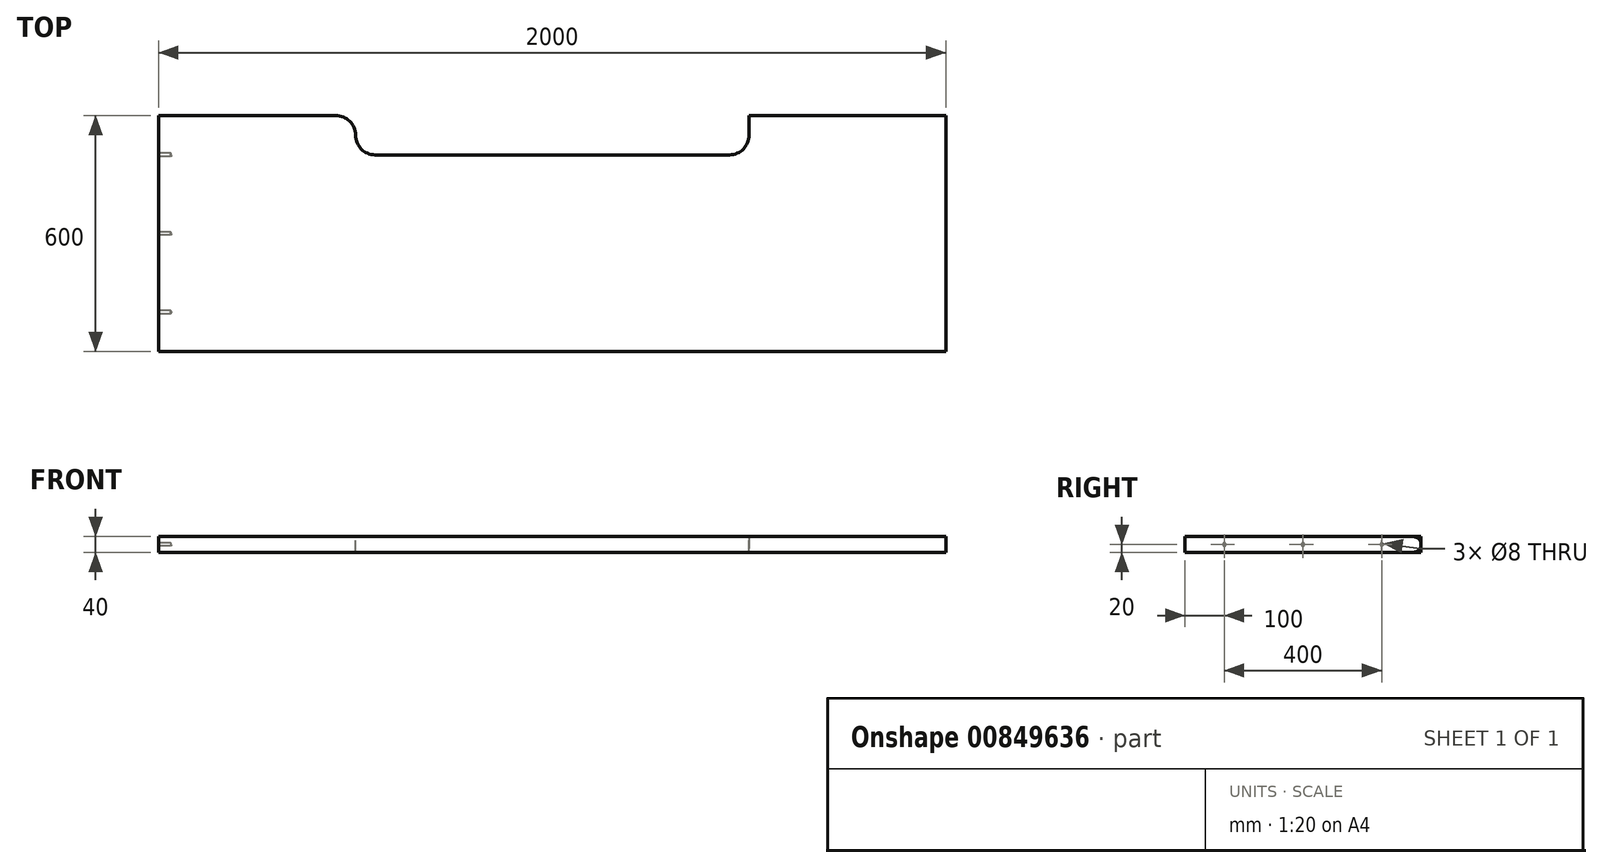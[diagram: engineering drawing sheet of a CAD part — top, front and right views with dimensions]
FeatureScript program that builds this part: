
annotation { "Feature Type Name" : "Feature", "Feature Type Description" : "" }
export const myFeature = defineFeature(function(context is Context, id is Id, definition is map)
    precondition{}
    {
        {
            var Q0;
            Q0=qCreatedBy(makeId("Top.planeOp"),FACE);
            var sketch = newSketch(context, id + "F0", { "sketchPlane" : qUnion([Q0])});
            skLineSegment(sketch, "E0.bottom", {"start": v(1000, -300) * mm, "end": v(-1000, -300) * mm});
            skLineSegment(sketch, "E0.top", {"start": v(1000, 300) * mm, "end": v(-1000, 300) * mm});
            skLineSegment(sketch, "E0.left", {"start": v(1000, -300) * mm, "end": v(1000, 300) * mm});
            skLineSegment(sketch, "E0.right", {"start": v(-1000, -300) * mm, "end": v(-1000, 300) * mm});
            skPoint(sketch, "E0.middle", {"position": v(0, 0) * mm});
            skSolve(sketch);
        }
        {
            var Q0;
            Q0=makeQuery(id+"F0.imprint","IMPRINT",FACE,{"disambiguationData":[TD([[makeQuery(id+"F0.imprint","IMPRINT",EDGE,{"derivedFrom":sQuery(id+"F0.wireOp",EDGE,"E0.bottom")}),-1.0]])]});
            extrude(context, id + "F1", {"entities" : qUnion([Q0]), "endBound" : BoundingType.SYMMETRIC, "depth" : 40 * mm, "offsetDistance" : 25 * mm, "hasSecondDirection" : true, "secondDirectionOppositeDirection" : true, "secondDirectionDepth" : 25 * mm});
        }
        {
            var Q0;
            Q0=makeQuery(id+"F1.opExtrude","SWEPT_FACE",FACE,{"disambiguationData":[OSD([sQuery(id+"F0.wireOp",EDGE,"E0.right")])]});
            var sketch = newSketch(context, id + "F2", { "sketchPlane" : qUnion([Q0])});
            skLineSegment(sketch, "E1", {"start": v(-300, 0) * mm, "end": v(300, 0) * mm});
            skPoint(sketch, "E2", {"position": v(-200, 0) * mm});
            skPoint(sketch, "E3", {"position": v(0, 0) * mm});
            skPoint(sketch, "E4", {"position": v(200, 0) * mm});
            skSolve(sketch);
        }
        {
            var Q0;
            Q0=sQuery(id+"F2.wireOp",VERTEX,"E2");
            var Q1;
            Q1=sQuery(id+"F2.wireOp",VERTEX,"E3");
            var Q2;
            Q2=sQuery(id+"F2.wireOp",VERTEX,"E4");
            var Q3;
            Q3=makeQuery(id+"F1.opExtrude","SWEPT_BODY",BODY,{"disambiguationData":[OSD([sQuery(id+"F0.wireOp",EDGE,"E0.bottom"),sQuery(id+"F0.wireOp",EDGE,"E0.top"),sQuery(id+"F0.wireOp",EDGE,"E0.left"),sQuery(id+"F0.wireOp",EDGE,"E0.right")])]});
            hole(context, id + "F3", {"style" : HoleStyle.SIMPLE, "endStyle" : HoleEndStyle.BLIND, "holeDiameter" : 8 * mm, "majorDiameter" : 5 * mm, "holeDepth" : 30 * mm, "isTappedThrough" : true, "tappedDepth" : 12 * mm, "tapClearance" : 3, "locations" : qUnion([Q0, Q1, Q2]), "scope" : qUnion([Q3])});
        }
        {
            var Q0;
            Q0=makeQuery(id+"F1.opExtrude","CAP_FACE",FACE,{"disambiguationData":[OSD([sQuery(id+"F0.wireOp",EDGE,"E0.bottom"),sQuery(id+"F0.wireOp",EDGE,"E0.top"),sQuery(id+"F0.wireOp",EDGE,"E0.left"),sQuery(id+"F0.wireOp",EDGE,"E0.right")])],"isStart":false});
            var sketch = newSketch(context, id + "F4", { "sketchPlane" : qUnion([Q0])});
            skLineSegment(sketch, "E5.bottom", {"start": v(500, 300) * mm, "end": v(-500, 300) * mm});
            skLineSegment(sketch, "E5.top", {"start": v(500, 200) * mm, "end": v(-500, 200) * mm});
            skLineSegment(sketch, "E5.left", {"start": v(500, 300) * mm, "end": v(500, 200) * mm});
            skLineSegment(sketch, "E5.right", {"start": v(-500, 300) * mm, "end": v(-500, 200) * mm});
            skSolve(sketch);
        }
        {
            var Q0;
            Q0=makeQuery(id+"F4.imprint","IMPRINT",FACE,{"disambiguationData":[TD([[makeQuery(id+"F4.imprint","IMPRINT",EDGE,{"derivedFrom":sQuery(id+"F4.wireOp",EDGE,"E5.bottom")}),1.0]])]});
            extrude(context, id + "F5", {"entities" : qUnion([Q0]), "operationType" : NewBodyOperationType.REMOVE, "endBound" : BoundingType.UP_TO_NEXT, "oppositeDirection" : true, "depth" : 25 * mm, "offsetDistance" : 25 * mm});
        }
        {
            var Q0;
            Q0=makeQuery(id+"F5.boolean.opBoolean","COPY",EDGE,{"derivedFrom":makeQuery(id+"F5.opExtrude","SWEPT_EDGE",EDGE,{"disambiguationData":[OSD([sQuery(id+"F0.wireOp",EDGE,"E0.top"),sQuery(id+"F4.wireOp",EDGE,"E5.bottom"),sQuery(id+"F4.wireOp",EDGE,"E5.left")])]})});
            var Q1;
            Q1=makeQuery(id+"F5.boolean.opBoolean","COPY",EDGE,{"derivedFrom":makeQuery(id+"F5.opExtrude","SWEPT_EDGE",EDGE,{"disambiguationData":[OSD([sQuery(id+"F4.wireOp",EDGE,"E5.top"),sQuery(id+"F4.wireOp",EDGE,"E5.left")])]})});
            var Q2;
            Q2=makeQuery(id+"F5.boolean.opBoolean","COPY",EDGE,{"derivedFrom":makeQuery(id+"F5.opExtrude","SWEPT_EDGE",EDGE,{"disambiguationData":[OSD([sQuery(id+"F4.wireOp",EDGE,"E5.top"),sQuery(id+"F4.wireOp",EDGE,"E5.right")])]})});
            var Q3;
            Q3=makeQuery(id+"F5.boolean.opBoolean","COPY",EDGE,{"derivedFrom":makeQuery(id+"F5.opExtrude","SWEPT_EDGE",EDGE,{"disambiguationData":[OSD([sQuery(id+"F0.wireOp",EDGE,"E0.top"),sQuery(id+"F4.wireOp",EDGE,"E5.bottom"),sQuery(id+"F4.wireOp",EDGE,"E5.right")])]})});
            fillet(context, id + "F6", {"entities" : qUnion([Q0, Q1, Q2, Q3]), "radius" : 50 * mm, "tangentPropagation" : true, "allowEdgeOverflow" : false});
        }
        {
            var Q0;
            {var subQ0=sQuery(id+"F0.wireOp",EDGE,"E0.left");var subQ1=sQuery(id+"F0.wireOp",EDGE,"E0.top");Q0=makeQuery(id+"F5.boolean.opBoolean","SPLIT",EDGE,{"disambiguationData":[TD([makeQuery(id+"F1.opExtrude","SWEPT_FACE",FACE,{"disambiguationData":[OSD([subQ0])]})])],"derivedFrom":makeQuery(id+"F1.opExtrude","CAP_EDGE",EDGE,{"disambiguationData":[OSD([subQ1])],"isStart":true})});}
            var Q1;
            {var subQ0=sQuery(id+"F0.wireOp",EDGE,"E0.left");var subQ1=sQuery(id+"F0.wireOp",EDGE,"E0.top");Q1=makeQuery(id+"F5.boolean.opBoolean","SPLIT",EDGE,{"disambiguationData":[TD([makeQuery(id+"F1.opExtrude","SWEPT_FACE",FACE,{"disambiguationData":[OSD([subQ0])]})])],"derivedFrom":makeQuery(id+"F1.opExtrude","CAP_EDGE",EDGE,{"disambiguationData":[OSD([subQ1])],"isStart":false})});}
            fillet(context, id + "F7", {"entities" : qUnion([Q0, Q1]), "radius" : 20 * mm, "tangentPropagation" : true, "allowEdgeOverflow" : false});
        }
    });
